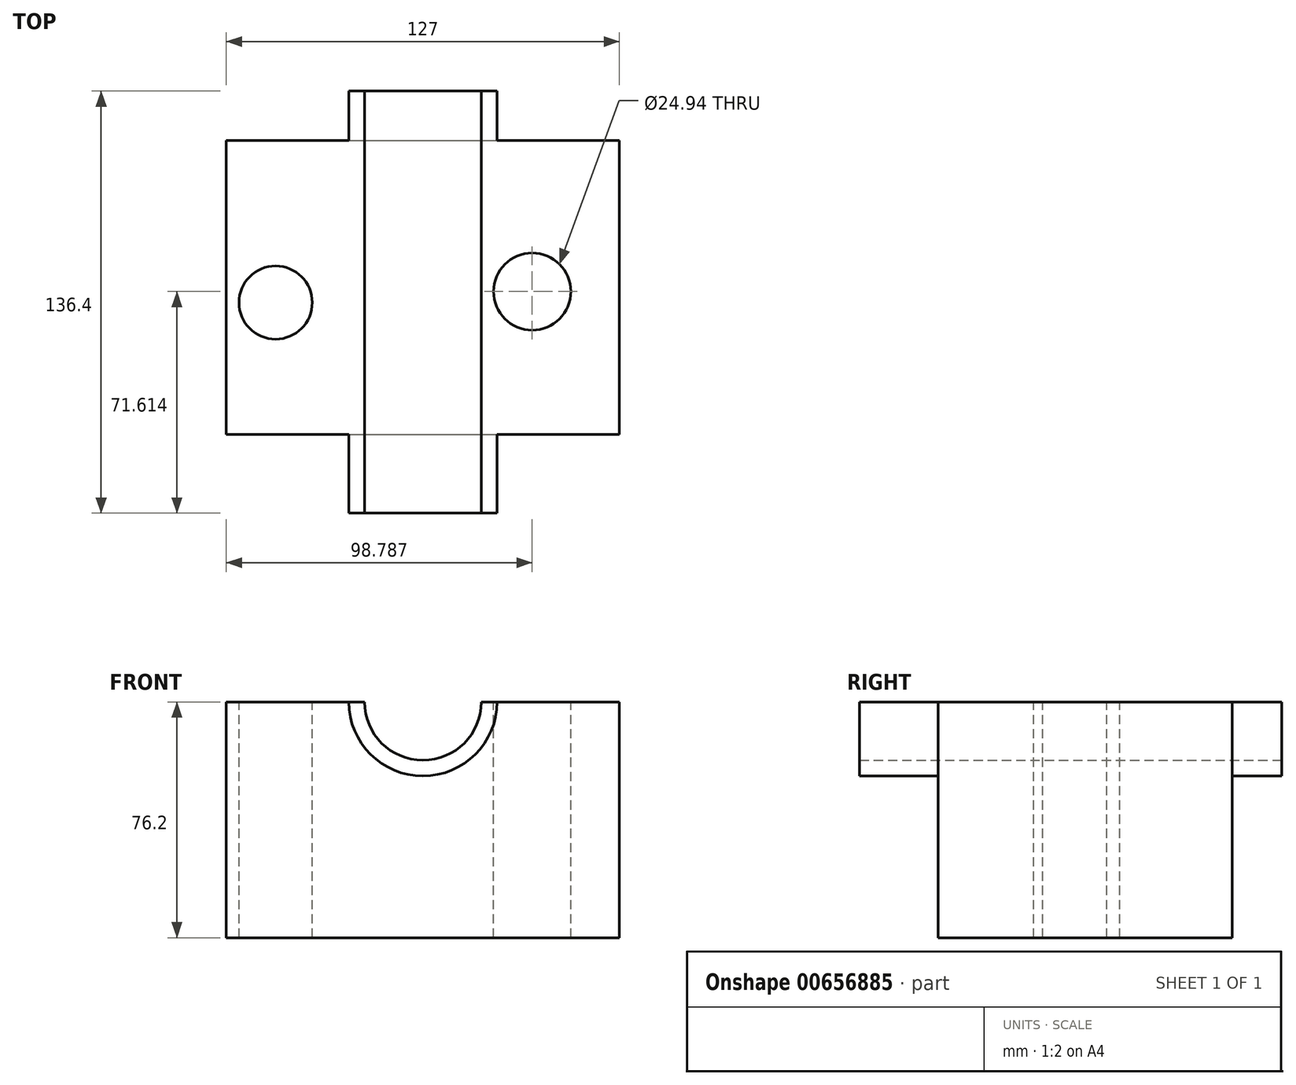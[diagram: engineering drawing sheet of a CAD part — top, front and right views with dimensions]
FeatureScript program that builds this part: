
annotation { "Feature Type Name" : "Feature", "Feature Type Description" : "" }
export const myFeature = defineFeature(function(context is Context, id is Id, definition is map)
    precondition{}
    {
        {
            var Q0;
            Q0=qCreatedBy(makeId("Front.planeOp"),FACE);
            var sketch = newSketch(context, id + "F0", { "sketchPlane" : qUnion([Q0])});
            skLineSegment(sketch, "E0.bottom", {"start": v(-60.54, 42.37) * mm, "end": v(66.46, 42.37) * mm});
            skLineSegment(sketch, "E0.top", {"start": v(-60.54, -33.83) * mm, "end": v(66.46, -33.83) * mm});
            skLineSegment(sketch, "E0.left", {"start": v(-60.54, 42.37) * mm, "end": v(-60.54, -33.83) * mm});
            skLineSegment(sketch, "E0.right", {"start": v(66.46, 42.37) * mm, "end": v(66.46, -33.83) * mm});
            skSolve(sketch);
        }
        {
            var Q0;
            Q0=qSketchRegion(id+"F0",true);
            extrude(context, id + "F1", {"entities" : qUnion([Q0]), "depth" : 95 * mm, "offsetDistance" : 25.4 * mm});
        }
        {
            var Q0;
            Q0=makeQuery(id+"F1.opExtrude","CAP_FACE",FACE,{"disambiguationData":[OSD([sQuery(id+"F0.wireOp",EDGE,"E0.bottom"),sQuery(id+"F0.wireOp",EDGE,"E0.top"),sQuery(id+"F0.wireOp",EDGE,"E0.left"),sQuery(id+"F0.wireOp",EDGE,"E0.right")])],"isStart":false});
            var sketch = newSketch(context, id + "F2", { "sketchPlane" : qUnion([Q0])});
            skCircle(sketch, "E1", {"center": v(2.96, 42.37) * mm, "radius": 18.87 * mm});
            skCircle(sketch, "E2", {"center": v(2.96, 42.37) * mm, "radius": 23.95 * mm});
            skSolve(sketch);
        }
        {
            var Q0;
            {var subQ0=sQuery(id+"F2.wireOp",EDGE,"E1");var subQ1=makeQuery(id+"F1.opExtrude","CAP_EDGE",EDGE,{"disambiguationData":[OSD([sQuery(id+"F0.wireOp",EDGE,"E0.bottom")])],"isStart":false});var subQ2=makeQuery(id+"F2.imprint","INTERSECT",VERTEX,{"disambiguationData":[OD(0.0)],"derivedFrom":[subQ1,subQ0]});Q0=makeQuery(id+"F2.imprint","IMPRINT",FACE,{"disambiguationData":[TD([[makeQuery(id+"F2.imprint","IMPRINT",EDGE,{"disambiguationData":[TD([[subQ2,-1.0]])],"derivedFrom":subQ0}),-1.0]])]});}
            extrude(context, id + "F3", {"entities" : qUnion([Q0]), "operationType" : NewBodyOperationType.ADD, "depth" : 25.4 * mm, "offsetDistance" : 25.4 * mm});
        }
        {
            var Q0;
            {var subQ0=sQuery(id+"F0.wireOp",EDGE,"E0.bottom");var subQ1=sQuery(id+"F2.wireOp",EDGE,"E1");Q0=makeQuery(id+"F3.boolean.opBoolean","SPLIT",FACE,{"disambiguationData":[TD([makeQuery(id+"F3.opExtrude","SWEPT_FACE",FACE,{"disambiguationData":[OSD([subQ1])]})])],"derivedFrom":makeQuery(id+"F1.opExtrude","CAP_FACE",FACE,{"disambiguationData":[OSD([subQ0,sQuery(id+"F0.wireOp",EDGE,"E0.top"),sQuery(id+"F0.wireOp",EDGE,"E0.left"),sQuery(id+"F0.wireOp",EDGE,"E0.right")])],"isStart":false})});}
            extrude(context, id + "F4", {"entities" : qUnion([Q0]), "operationType" : NewBodyOperationType.REMOVE, "oppositeDirection" : true, "depth" : 115.82 * mm, "offsetDistance" : 25.4 * mm});
        }
        {
            var Q0;
            {var subQ0=sQuery(id+"F2.wireOp",EDGE,"E1");var subQ1=makeQuery(id+"F1.opExtrude","CAP_EDGE",EDGE,{"disambiguationData":[OSD([sQuery(id+"F0.wireOp",EDGE,"E0.bottom")])],"isStart":false});var subQ2=makeQuery(id+"F2.imprint","INTERSECT",VERTEX,{"disambiguationData":[OD(0.0)],"derivedFrom":[subQ1,subQ0]});Q0=makeQuery(id+"F2.imprint","IMPRINT",FACE,{"disambiguationData":[TD([[makeQuery(id+"F2.imprint","IMPRINT",EDGE,{"disambiguationData":[TD([[subQ2,-1.0]])],"derivedFrom":subQ0}),-1.0]])]});}
            extrude(context, id + "F5", {"entities" : qUnion([Q0]), "operationType" : NewBodyOperationType.ADD, "oppositeDirection" : true, "depth" : 111 * mm, "offsetDistance" : 25.4 * mm});
        }
        {
            var Q0;
            {var subQ0=sQuery(id+"F2.wireOp",EDGE,"E2");var subQ1=sQuery(id+"F0.wireOp",EDGE,"E0.bottom");var subQ2=makeQuery(id+"F1.opExtrude","CAP_EDGE",EDGE,{"disambiguationData":[OSD([subQ1])],"isStart":false});var subQ4=makeQuery(id+"F2.imprint","IMPRINT",EDGE,{"disambiguationData":[TD([[makeQuery(id+"F2.imprint","INTERSECT",VERTEX,{"disambiguationData":[OD(0.0)],"derivedFrom":[subQ2,subQ0]}),-1.0]])],"derivedFrom":subQ2});var subQ6=sQuery(id+"F0.wireOp",EDGE,"E0.left");Q0=makeQuery(id+"F5.boolean.opBoolean","MERGE",FACE,{"derivedFrom":[makeQuery(id+"F4.boolean.opBoolean","SPLIT",FACE,{"disambiguationData":[TD([makeQuery(id+"F1.opExtrude","SWEPT_FACE",FACE,{"disambiguationData":[OSD([subQ6])]})])],"derivedFrom":makeQuery(id+"F3.boolean.opBoolean","MERGE",FACE,{"derivedFrom":[makeQuery(id+"F1.opExtrude","SWEPT_FACE",FACE,{"disambiguationData":[OSD([subQ1])]}),makeQuery(id+"F3.opExtrude","SWEPT_FACE",FACE,{"disambiguationData":[OSD([subQ1]),TDD([subQ4])]}),makeQuery(id+"F3.opExtrude","SWEPT_FACE",FACE,{"disambiguationData":[OSD([subQ1]),TDD([makeQuery(id+"F2.imprint","IMPRINT",EDGE,{"disambiguationData":[TD([[makeQuery(id+"F2.imprint","INTERSECT",VERTEX,{"disambiguationData":[OD(1.0)],"derivedFrom":[subQ2,subQ0]}),1.0]])],"derivedFrom":subQ2})])]})]})}),makeQuery(id+"F5.opExtrude","SWEPT_FACE",FACE,{"disambiguationData":[OSD([subQ1]),TDD([subQ4])]})]});}
            var sketch = newSketch(context, id + "F6", { "sketchPlane" : qUnion([Q0])});
            skCircle(sketch, "E3", {"center": v(-44.63, -52.35) * mm, "radius": 11.84 * mm});
            skSolve(sketch);
        }
        {
            var Q0;
            Q0=qSketchRegion(id+"F6",true);
            extrude(context, id + "F7", {"entities" : qUnion([Q0]), "operationType" : NewBodyOperationType.REMOVE, "oppositeDirection" : true, "depth" : 300.74 * mm, "offsetDistance" : 25.4 * mm});
        }
        {
            var Q0;
            {var subQ0=sQuery(id+"F2.wireOp",EDGE,"E2");var subQ1=sQuery(id+"F0.wireOp",EDGE,"E0.bottom");var subQ2=makeQuery(id+"F1.opExtrude","CAP_EDGE",EDGE,{"disambiguationData":[OSD([subQ1])],"isStart":false});var subQ4=makeQuery(id+"F2.imprint","IMPRINT",EDGE,{"disambiguationData":[TD([[makeQuery(id+"F2.imprint","INTERSECT",VERTEX,{"disambiguationData":[OD(1.0)],"derivedFrom":[subQ2,subQ0]}),1.0]])],"derivedFrom":subQ2});var subQ5=sQuery(id+"F0.wireOp",EDGE,"E0.right");Q0=makeQuery(id+"F5.boolean.opBoolean","MERGE",FACE,{"derivedFrom":[makeQuery(id+"F4.boolean.opBoolean","SPLIT",FACE,{"disambiguationData":[TD([makeQuery(id+"F1.opExtrude","SWEPT_FACE",FACE,{"disambiguationData":[OSD([subQ5])]})])],"derivedFrom":makeQuery(id+"F3.boolean.opBoolean","MERGE",FACE,{"derivedFrom":[makeQuery(id+"F1.opExtrude","SWEPT_FACE",FACE,{"disambiguationData":[OSD([subQ1])]}),makeQuery(id+"F3.opExtrude","SWEPT_FACE",FACE,{"disambiguationData":[OSD([subQ1]),TDD([makeQuery(id+"F2.imprint","IMPRINT",EDGE,{"disambiguationData":[TD([[makeQuery(id+"F2.imprint","INTERSECT",VERTEX,{"disambiguationData":[OD(0.0)],"derivedFrom":[subQ2,subQ0]}),-1.0]])],"derivedFrom":subQ2})])]}),makeQuery(id+"F3.opExtrude","SWEPT_FACE",FACE,{"disambiguationData":[OSD([subQ1]),TDD([subQ4])]})]})}),makeQuery(id+"F5.opExtrude","SWEPT_FACE",FACE,{"disambiguationData":[OSD([subQ1]),TDD([subQ4])]})]});}
            var sketch = newSketch(context, id + "F8", { "sketchPlane" : qUnion([Q0])});
            skCircle(sketch, "E4", {"center": v(38.25, -48.79) * mm, "radius": 12.47 * mm});
            skSolve(sketch);
        }
        {
            var Q0;
            Q0=qSketchRegion(id+"F8",true);
            extrude(context, id + "F9", {"entities" : qUnion([Q0]), "operationType" : NewBodyOperationType.REMOVE, "oppositeDirection" : true, "depth" : 188.47 * mm, "offsetDistance" : 25.4 * mm});
        }
    });
